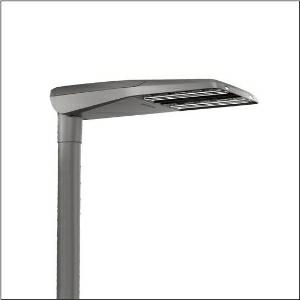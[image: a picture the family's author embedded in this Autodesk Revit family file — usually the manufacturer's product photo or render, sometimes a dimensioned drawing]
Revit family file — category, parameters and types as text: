
# Revit family: streetlight_sl_11_iq_midi___st1_2a_5xc3a31f08me_35e9
name_source: partatom
category: Lighting Fixtures
units: mm (PartAtom-declared; Revit-internal decimal feet)

## family parameters
Cut with Voids When Loaded = No
Host = Face
Light Source = No
Part Type = Normal
Room Calculation Point = No
Round Connector Dimension = Use Diameter
Shared = No

## types (1)
- --- (1 x LED, 15580 lm, 124.7 W, 3000K)
    Apparent Load = 125 VA
    CIE Flux Codes = 32 70 96 100 100
    Color Rendering = 80
    Color Temperature = 3000K
    Default Elevation = 1800 mm
    Description = Streetlight SL 11 iQ midi, mast luminaire, primary light control with 3 zone facetted reflector, of plastic, silver coated, highly specular, primary optical cover: cover, of PMMA, transparent, light distribution: ST1.2a, light emission: direct distribution, primary light characteristic: asymmetric, installation type: post-top, side-entry, lamps: LED, High Power LED, rated values: 15.580lm | 124,7W | 124,9lm/W (begin service life); end service life: 15.580lm | 132,2W; at 50% lumin. flux: 7.790lm | 57,1W | 136,4lm/W, colour temperature: 3000K, colour rendering: CRI > 80, light colour: 830, light setting 1 begin service life: 100% | 15.580lm | 124,7W | 124,9lm/W | 3.000K, light setting 1 end service life: 132,2W, further light settings possible, control: Street-Remote, optimised constant luminous flux control (CLO 2.0), Desk-Remote (wireless, voltage-free reading and setting of iQ features in the workshop via application-optimized NFC function/RFID function), Light-Fading, Smart-Wire, Night-Set, Lumen-Switch, Temp-Guard, Auto-Match, with cable H07RN-F 5x 1.5mm², mains connection: 230..240V, AC, 50/60Hz, connection cable pre-assembled, cable length: 12,5m, luminaire housing, of diecast aluminium, powder-coated, Siteco® metallic grey (DB 702S), please order mast flange separately, inclination adjustable without tools: 0°, 5°, 10°, 15° (post-top) | 0°, -5°, -10°, -15° (side-entry), sealing non-destructively replaceable, multi-level sealing system, length: 780mm, width: 376mm, height: 118mm, mast flange for spigot size: 42mm (side-entry): 5XC10008XM4, 60/48mm (side-entry/post-top): 5XC10108XM2, 76/60mm (side-entry/post-top): 5XC10108XM1, equipment: Power, protection rating (complete): IP66, insulation class (complete): insulation class II (safety insulation), certification: CE, ENEC, ENEC+, VDE, impact resistance: IK10, permissible operating ambient temperature for outdoor applications: -25..+50°C, standard-compliant lighting for roads and squares, Environmental Product Declaration (EPD) tested and certified by an independent institute, packaging unit: 1 piece

Light Distribution: ST1.2a
    Height = 118 mm
    Lamp = 1 x LED
    Lamp Light Flux = 15580 lm
    Lamp Power = 124.7 W
    Lamp count = 1
    Length = 780 mm
    Luminous efficacy = 125 lm/W
    Manufacturer = Siteco
    ModVariant = No
    Model = 5XC3A31F08ME
    Number of Poles = 1
    OnlyDefault = Yes
    Power Factor = 1
    Product Name = Streetlight SL 11 iQ midi | ST1.2a
    Product group = mast luminaire | pylon top
    ProductGroupID = 6100
    Protection Class = Protection class II
    Protection Degree = IP 66
    RLX_Detail_Level = 1
    RLX_Emergency_Light_Flux = 0 lm
    RLX_Emergency_Type = 0
    RLX_Emergency_Type_DB = No
    RlxData = <blob elided: 70985 chars, md5=62d58614>
    Socket = socket
    Standby Power = 0 W
    System Light Flux = 15580 lm
    System Power = 125 W
    Type Comments = factory setting: luminous flux: 100 % | dim-lin: 254 | 557 mA
    Type Image = l_1005960.jpg
    URL = http://relux.com
    VarID = @adj_217483
    Voltage = 0 V
    Weight = 0.00 kg
    Width = 376 mm

## geometry (parser evidence)
native form markers: Blend x4, Sweep x12
no freeform markers — native parametric forms only
